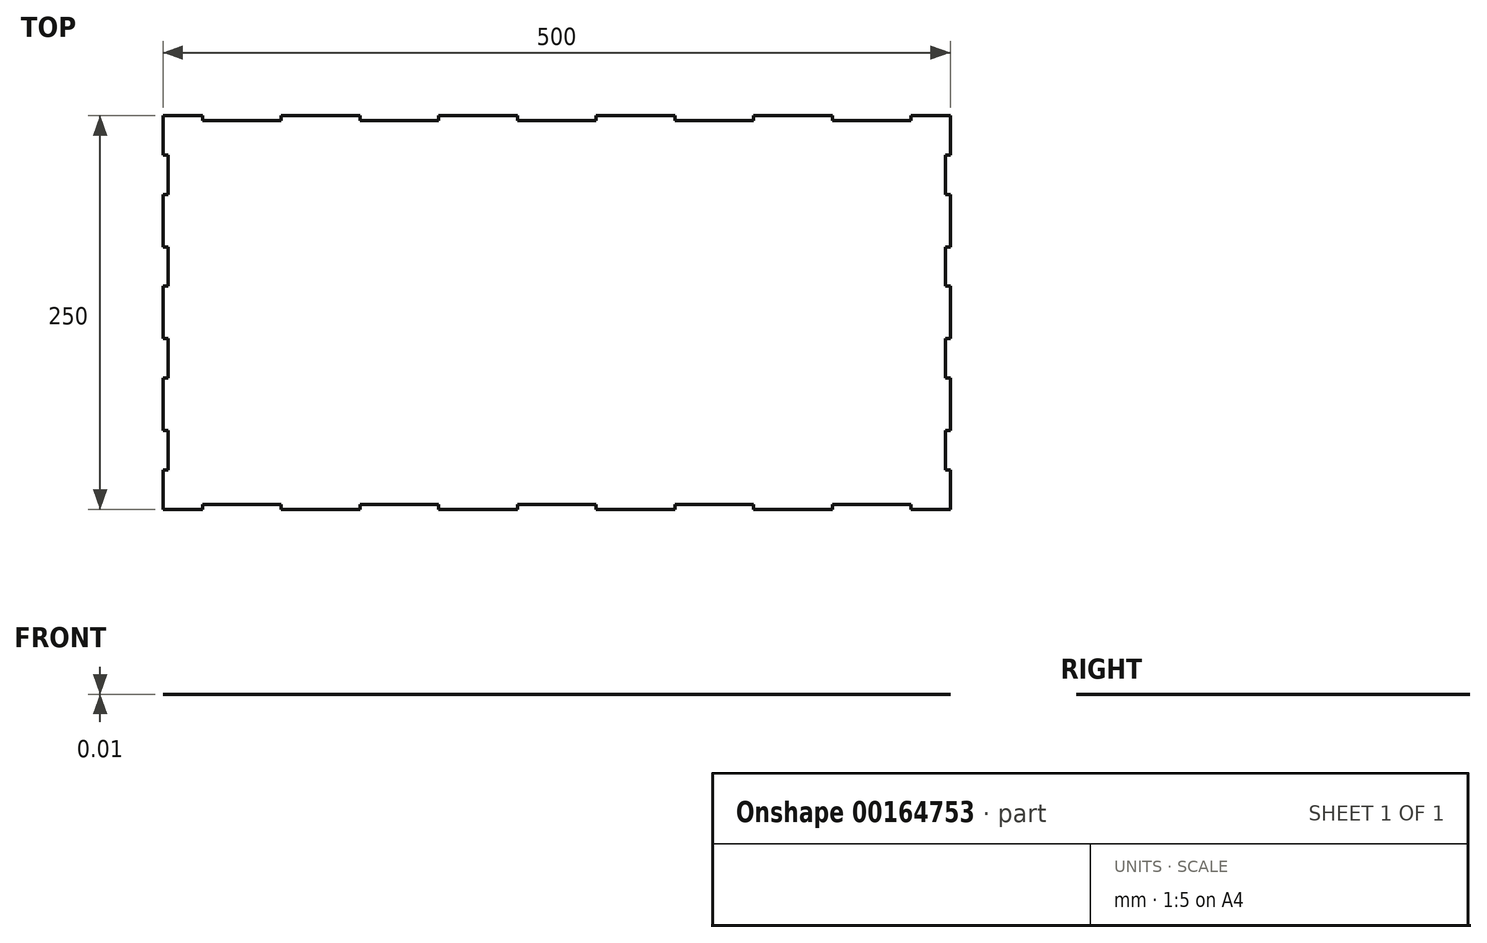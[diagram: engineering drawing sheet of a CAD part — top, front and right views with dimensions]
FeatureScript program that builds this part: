
annotation { "Feature Type Name" : "Feature", "Feature Type Description" : "" }
export const myFeature = defineFeature(function(context is Context, id is Id, definition is map)
    precondition{}
    {
        {
            var Q0;
            Q0=qCreatedBy(makeId("Top.planeOp"),FACE);
            var sketch = newSketch(context, id + "F0", { "sketchPlane" : qUnion([Q0])});
            skLineSegment(sketch, "E0.bottom", {"start": v(-250, 125) * mm, "end": v(250, 125) * mm});
            skLineSegment(sketch, "E0.top", {"start": v(-250, -125) * mm, "end": v(250, -125) * mm});
            skLineSegment(sketch, "E0.left", {"start": v(-250, 125) * mm, "end": v(-250, -125) * mm});
            skLineSegment(sketch, "E0.right", {"start": v(250, 125) * mm, "end": v(250, -125) * mm});
            skPoint(sketch, "E0.middle", {"position": v(0, 0) * mm});
            skSolve(sketch);
        }
        {
            var Q0;
            Q0 = qSketchRegion(id + "F0", true);
            extrude(context, id + "F1", {"entities" : qUnion([Q0]), "depth" : 1 / 101.6 * mm});
        }
        {
            var Q0;
            Q0=makeQuery(id+"F1.opExtrude","CAP_FACE",FACE,{"disambiguationData":[OSD([sQuery(id+"F0.wireOp",EDGE,"E0.bottom"),sQuery(id+"F0.wireOp",EDGE,"E0.top"),sQuery(id+"F0.wireOp",EDGE,"E0.left"),sQuery(id+"F0.wireOp",EDGE,"E0.right")])],"isStart":false});
            var sketch = newSketch(context, id + "F2", { "sketchPlane" : qUnion([Q0])});
            skLineSegment(sketch, "E1.bottom", {"start": v(-225, 125) * mm, "end": v(-175, 125) * mm});
            skLineSegment(sketch, "E1.top", {"start": v(-225, 121.82) * mm, "end": v(-175, 121.82) * mm});
            skLineSegment(sketch, "E1.left", {"start": v(-225, 125) * mm, "end": v(-225, 121.82) * mm});
            skLineSegment(sketch, "E1.right", {"start": v(-175, 125) * mm, "end": v(-175, 121.82) * mm});
            skLineSegment(sketch, "E2.0.1.0", {"start": v(-225, -121.83) * mm, "end": v(-175, -121.83) * mm});
            skLineSegment(sketch, "E2.0.1.1", {"start": v(-225, -125) * mm, "end": v(-175, -125) * mm});
            skLineSegment(sketch, "E2.0.1.2", {"start": v(-225, -121.82) * mm, "end": v(-225, -125) * mm});
            skLineSegment(sketch, "E2.0.1.3", {"start": v(-175, -121.82) * mm, "end": v(-175, -125) * mm});
            skLineSegment(sketch, "E2.1.0.0", {"start": v(-125, 125) * mm, "end": v(-75, 125) * mm});
            skLineSegment(sketch, "E2.1.0.1", {"start": v(-125, 121.82) * mm, "end": v(-75, 121.82) * mm});
            skLineSegment(sketch, "E2.1.0.2", {"start": v(-125, 125) * mm, "end": v(-125, 121.82) * mm});
            skLineSegment(sketch, "E2.1.0.3", {"start": v(-75, 125) * mm, "end": v(-75, 121.82) * mm});
            skLineSegment(sketch, "E2.1.1.0", {"start": v(-125, -121.83) * mm, "end": v(-75, -121.83) * mm});
            skLineSegment(sketch, "E2.1.1.1", {"start": v(-125, -125) * mm, "end": v(-75, -125) * mm});
            skLineSegment(sketch, "E2.1.1.2", {"start": v(-125, -121.82) * mm, "end": v(-125, -125) * mm});
            skLineSegment(sketch, "E2.1.1.3", {"start": v(-75, -121.82) * mm, "end": v(-75, -125) * mm});
            skLineSegment(sketch, "E2.2.0.0", {"start": v(-25, 125) * mm, "end": v(25, 125) * mm});
            skLineSegment(sketch, "E2.2.0.1", {"start": v(-25, 121.82) * mm, "end": v(25, 121.82) * mm});
            skLineSegment(sketch, "E2.2.0.2", {"start": v(-25, 125) * mm, "end": v(-25, 121.82) * mm});
            skLineSegment(sketch, "E2.2.0.3", {"start": v(25, 125) * mm, "end": v(25, 121.82) * mm});
            skLineSegment(sketch, "E2.2.1.0", {"start": v(-25, -121.83) * mm, "end": v(25, -121.83) * mm});
            skLineSegment(sketch, "E2.2.1.1", {"start": v(-25, -125) * mm, "end": v(25, -125) * mm});
            skLineSegment(sketch, "E2.2.1.2", {"start": v(-25, -121.82) * mm, "end": v(-25, -125) * mm});
            skLineSegment(sketch, "E2.2.1.3", {"start": v(25, -121.82) * mm, "end": v(25, -125) * mm});
            skLineSegment(sketch, "E2.3.0.0", {"start": v(75, 125) * mm, "end": v(125, 125) * mm});
            skLineSegment(sketch, "E2.3.0.1", {"start": v(75, 121.82) * mm, "end": v(125, 121.82) * mm});
            skLineSegment(sketch, "E2.3.0.2", {"start": v(75, 125) * mm, "end": v(75, 121.82) * mm});
            skLineSegment(sketch, "E2.3.0.3", {"start": v(125, 125) * mm, "end": v(125, 121.82) * mm});
            skLineSegment(sketch, "E2.3.1.0", {"start": v(75, -121.83) * mm, "end": v(125, -121.83) * mm});
            skLineSegment(sketch, "E2.3.1.1", {"start": v(75, -125) * mm, "end": v(125, -125) * mm});
            skLineSegment(sketch, "E2.3.1.2", {"start": v(75, -121.82) * mm, "end": v(75, -125) * mm});
            skLineSegment(sketch, "E2.3.1.3", {"start": v(125, -121.82) * mm, "end": v(125, -125) * mm});
            skLineSegment(sketch, "E2.4.0.0", {"start": v(175, 125) * mm, "end": v(225, 125) * mm});
            skLineSegment(sketch, "E2.4.0.1", {"start": v(175, 121.82) * mm, "end": v(225, 121.82) * mm});
            skLineSegment(sketch, "E2.4.0.2", {"start": v(175, 125) * mm, "end": v(175, 121.82) * mm});
            skLineSegment(sketch, "E2.4.0.3", {"start": v(225, 125) * mm, "end": v(225, 121.82) * mm});
            skLineSegment(sketch, "E2.4.1.0", {"start": v(175, -121.83) * mm, "end": v(225, -121.83) * mm});
            skLineSegment(sketch, "E2.4.1.1", {"start": v(175, -125) * mm, "end": v(225, -125) * mm});
            skLineSegment(sketch, "E2.4.1.2", {"start": v(175, -121.82) * mm, "end": v(175, -125) * mm});
            skLineSegment(sketch, "E2.4.1.3", {"start": v(225, -121.82) * mm, "end": v(225, -125) * mm});
            skLineSegment(sketch, "E2.direction1", {"start": v(-225, 121.82) * mm, "end": v(-125, 121.82) * mm, "construction": true});
            skLineSegment(sketch, "E2.direction2", {"start": v(-225, 121.82) * mm, "end": v(-225, -125) * mm, "construction": true});
            skLineSegment(sketch, "E3.bottom", {"start": v(250, 100) * mm, "end": v(246.83, 100) * mm});
            skLineSegment(sketch, "E3.top", {"start": v(250, 75) * mm, "end": v(246.83, 75) * mm});
            skLineSegment(sketch, "E3.left", {"start": v(250, 100) * mm, "end": v(250, 75) * mm});
            skLineSegment(sketch, "E3.right", {"start": v(246.83, 100) * mm, "end": v(246.83, 75) * mm});
            skLineSegment(sketch, "E4.0.1.0", {"start": v(246.83, 41.67) * mm, "end": v(246.83, 16.67) * mm});
            skLineSegment(sketch, "E4.0.1.1", {"start": v(250, 41.67) * mm, "end": v(250, 16.67) * mm});
            skLineSegment(sketch, "E4.0.1.2", {"start": v(250, 41.67) * mm, "end": v(246.83, 41.67) * mm});
            skLineSegment(sketch, "E4.0.1.3", {"start": v(250, 16.67) * mm, "end": v(246.83, 16.67) * mm});
            skLineSegment(sketch, "E4.0.2.0", {"start": v(246.83, -16.67) * mm, "end": v(246.83, -41.67) * mm});
            skLineSegment(sketch, "E4.0.2.1", {"start": v(250, -16.67) * mm, "end": v(250, -41.67) * mm});
            skLineSegment(sketch, "E4.0.2.2", {"start": v(250, -16.67) * mm, "end": v(246.83, -16.67) * mm});
            skLineSegment(sketch, "E4.0.2.3", {"start": v(250, -41.67) * mm, "end": v(246.83, -41.67) * mm});
            skLineSegment(sketch, "E4.direction1", {"start": v(246.83, 75) * mm, "end": v(246.83, 75) * mm});
            skLineSegment(sketch, "E4.direction2", {"start": v(246.83, 75) * mm, "end": v(246.83, 41.67) * mm, "construction": true});
            skLineSegment(sketch, "E5.0.0.3", {"start": v(246.83, -75) * mm, "end": v(246.83, -100) * mm});
            skLineSegment(sketch, "E5.3.0.3", {"start": v(250, -75) * mm, "end": v(250, -100) * mm});
            skLineSegment(sketch, "E5.6.0.3", {"start": v(250, -75) * mm, "end": v(246.83, -75) * mm});
            skLineSegment(sketch, "E5.9.0.3", {"start": v(250, -100) * mm, "end": v(246.83, -100) * mm});
            skLineSegment(sketch, "E6.1.0.0", {"start": v(-250, -75) * mm, "end": v(-250, -100) * mm});
            skLineSegment(sketch, "E6.1.0.1", {"start": v(-250, 41.67) * mm, "end": v(-250, 16.67) * mm});
            skLineSegment(sketch, "E6.1.0.2", {"start": v(-250, -16.67) * mm, "end": v(-250, -41.67) * mm});
            skLineSegment(sketch, "E6.1.0.3", {"start": v(-250, 75) * mm, "end": v(-250, 41.67) * mm, "construction": true});
            skLineSegment(sketch, "E6.1.0.4", {"start": v(-246.82, 41.67) * mm, "end": v(-246.82, 16.67) * mm});
            skLineSegment(sketch, "E6.1.0.5", {"start": v(-246.82, -16.67) * mm, "end": v(-246.82, -41.67) * mm});
            skLineSegment(sketch, "E6.1.0.6", {"start": v(-246.82, 100) * mm, "end": v(-246.82, 75) * mm});
            skLineSegment(sketch, "E6.1.0.7", {"start": v(-246.82, -75) * mm, "end": v(-246.82, -100) * mm});
            skLineSegment(sketch, "E6.1.0.8", {"start": v(-250, 100) * mm, "end": v(-250, 75) * mm});
            skLineSegment(sketch, "E6.1.0.9", {"start": v(-246.82, -41.67) * mm, "end": v(-250, -41.67) * mm});
            skLineSegment(sketch, "E6.1.0.10", {"start": v(-246.82, 16.67) * mm, "end": v(-250, 16.67) * mm});
            skLineSegment(sketch, "E6.1.0.11", {"start": v(-246.83, 100) * mm, "end": v(-250, 100) * mm});
            skLineSegment(sketch, "E6.1.0.12", {"start": v(-246.82, -75) * mm, "end": v(-250, -75) * mm});
            skLineSegment(sketch, "E6.1.0.13", {"start": v(-246.82, -16.67) * mm, "end": v(-250, -16.67) * mm});
            skLineSegment(sketch, "E6.1.0.14", {"start": v(-246.83, -100) * mm, "end": v(-250, -100) * mm});
            skLineSegment(sketch, "E6.1.0.15", {"start": v(-246.82, 41.67) * mm, "end": v(-250, 41.67) * mm});
            skLineSegment(sketch, "E6.1.0.16", {"start": v(-246.82, 75) * mm, "end": v(-250, 75) * mm});
            skLineSegment(sketch, "E6.direction1", {"start": v(246.83, -100) * mm, "end": v(-250, -100) * mm, "construction": true});
            skSolve(sketch);
        }
        {
            var Q0;
            Q0 = qSketchRegion(id + "F2", true);
            extrude(context, id + "F3", {"entities" : qUnion([Q0]), "operationType" : NewBodyOperationType.REMOVE, "endBound" : BoundingType.THROUGH_ALL, "oppositeDirection" : true, "depth" : 25 * mm});
        }
    });
